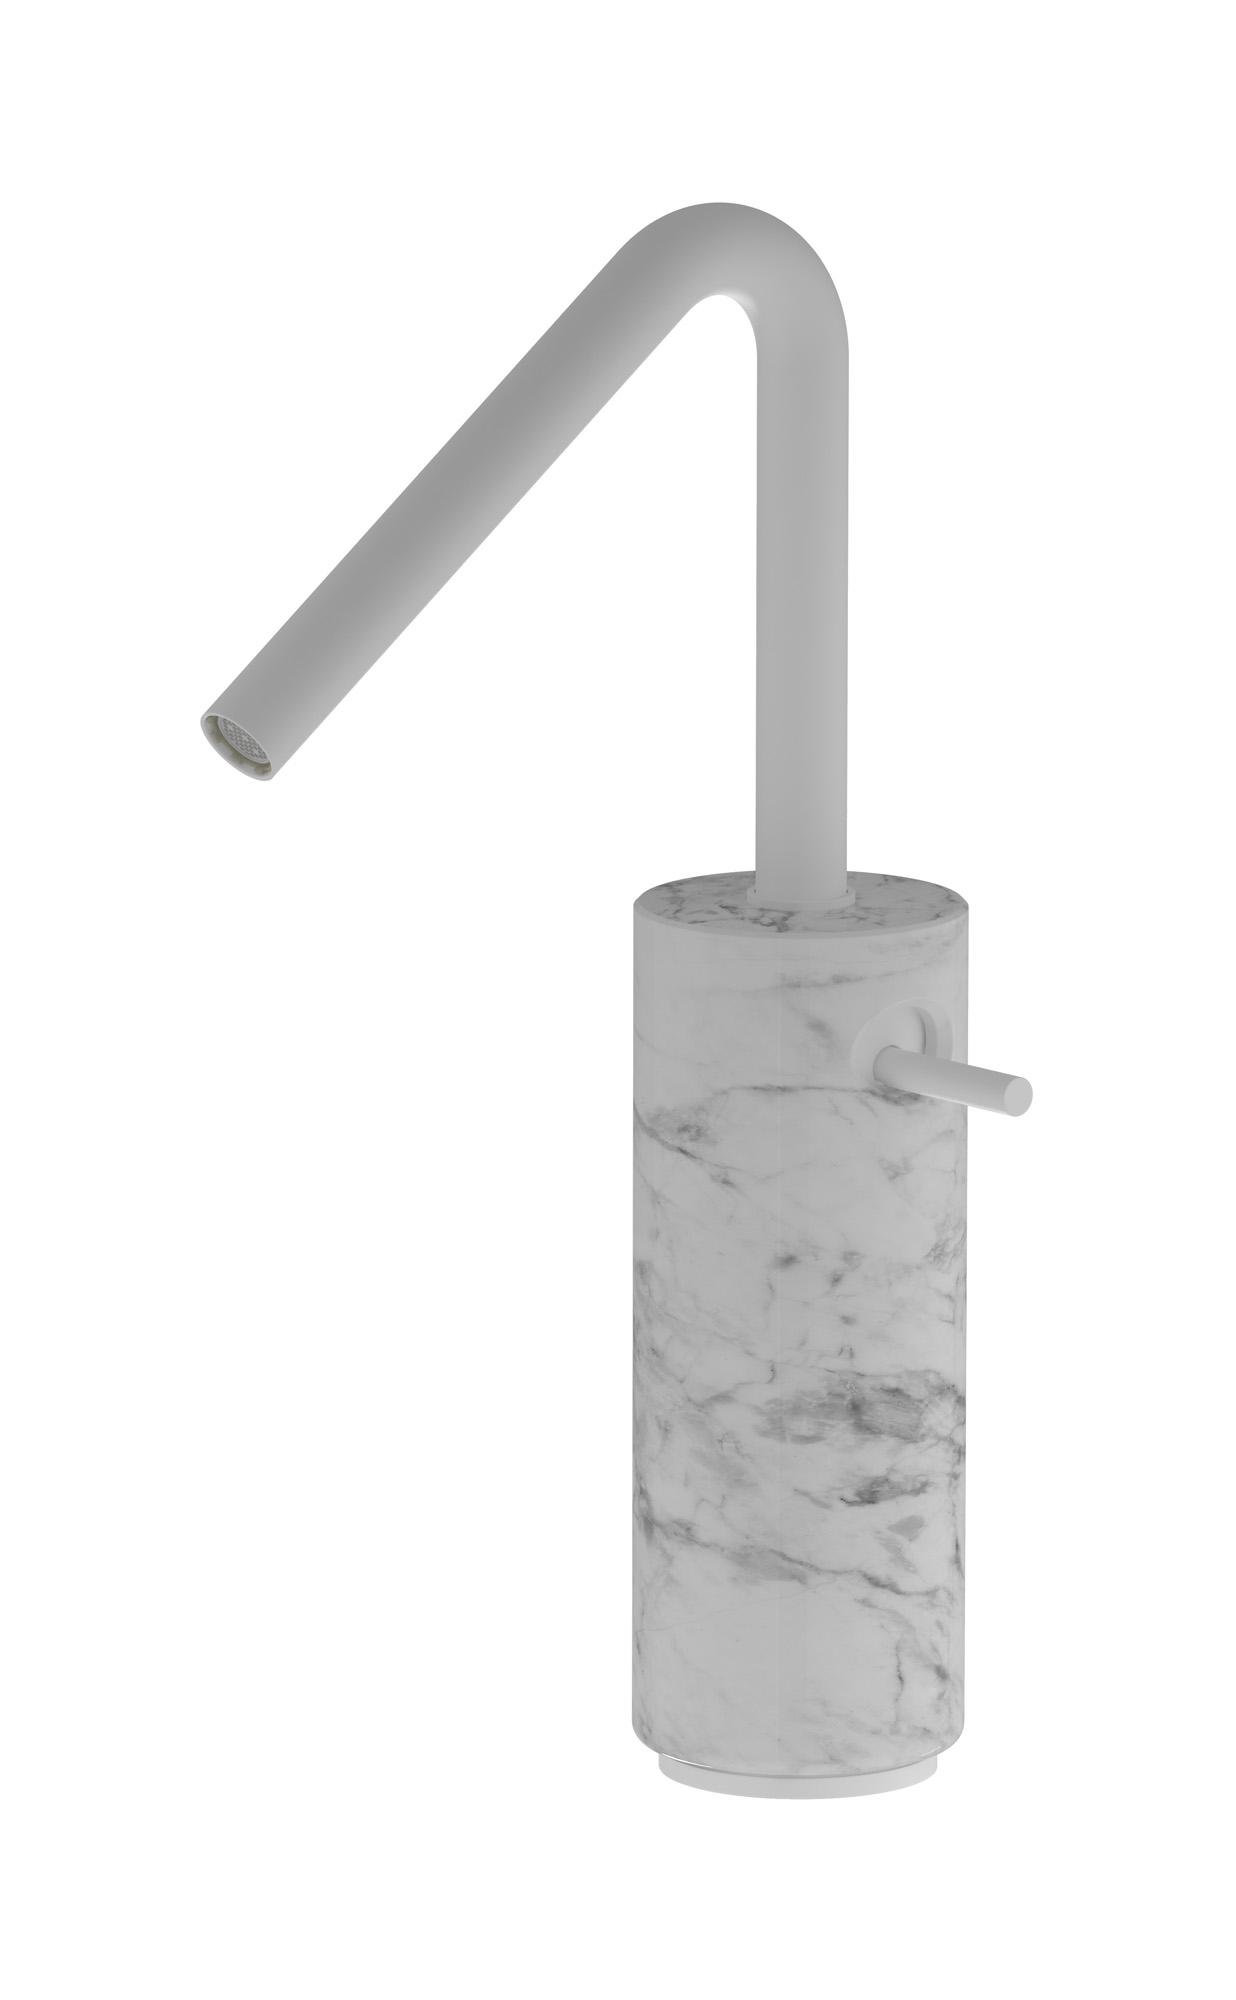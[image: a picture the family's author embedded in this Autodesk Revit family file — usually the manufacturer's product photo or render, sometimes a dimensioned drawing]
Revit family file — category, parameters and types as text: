
# Revit family: MR202_1
name_source: partatom
category: Apparecchi idraulici
units: mm (PartAtom-declared; Revit-internal decimal feet)

## family parameters
Basato su piano di lavoro = No
Condiviso = No
Mantieni orientamento annotazione = No
Numero OmniClass = 23.45.55.17
Punto di calcolo locali = No
Quota connettore circolare = Usa diametro
Sempre verticale = Sì
Taglio con vuoti quando caricato = No
Tipo di parte = Normale
Titolo OmniClass = Mixing Faucets

## types (14) — shared parameters
Cold water inlet = 10 mm  [stored 0.0328084 ft]
Commenti sul tipo = Washbasin mixer
Connessione CW = No
Connessione HW = No
Connessione di scarico = No
Connessione di ventilazione = No
Descrizione = Tall monohole washbasin mixer
Hot water inlet = 10 mm  [stored 0.0328084 ft]
Produttore = IB Rubinetterie S.p.A.
URL = https://www.weareib.it
zero-valued in all types: Prospetto di default

## per-type parameters (varying)
| type | Finishes surface | Immagine tipo | Modello |
| Chrome | IB_Chrome | MR202CC_1.jpg | MR202CC_1 |
| Platinum | IB_Platinum | MR202PL_1.jpg | MR202PL_1 |
| Brushed nickel | IB_Brushed nickel | MR202SS_1.jpg | MR202SS_1 |
| Natural brass | IB_Brass | MR202ON_1.jpg | MR202ON_1 |
| Matt white | IB_matt white | MR202BO_1.jpg | MR202BO_1 |
| Matt black | IB_matt black | MR202NP_1.jpg | MR202NP_1 |
| Black chrome | IB_Black chrome | MR202CF_1.jpg | MR202CF_1 |
| Brushed black chrome | IB_Brushed black chrome | MR202CS_1.jpg | MR202CS_1 |
| Pale gold | IB_Pale gold | MR202II_1.jpg | MR202II_1 |
| Brushed pale gold | IB_brushed pale gold | MR202IS_1.jpg | MR202IS_1 |
| Rose gold | IB_Rose gold | MR202RS_1.jpg | MR202RS_1 |
| Brushed rose gold | IB_Brushed rose gold | MR202SR_1.jpg | MR202SR_1 |
| Gold | IB_gold | MR202OO_1.jpg | MR202OO_1 |
| Brushed gold | IB_brushed gold | MR202OS_1.jpg | MR202OS_1 |

note: [stored X ft] marks values corroborated as IEEE doubles in the binary element streams (Revit-internal decimal feet)
